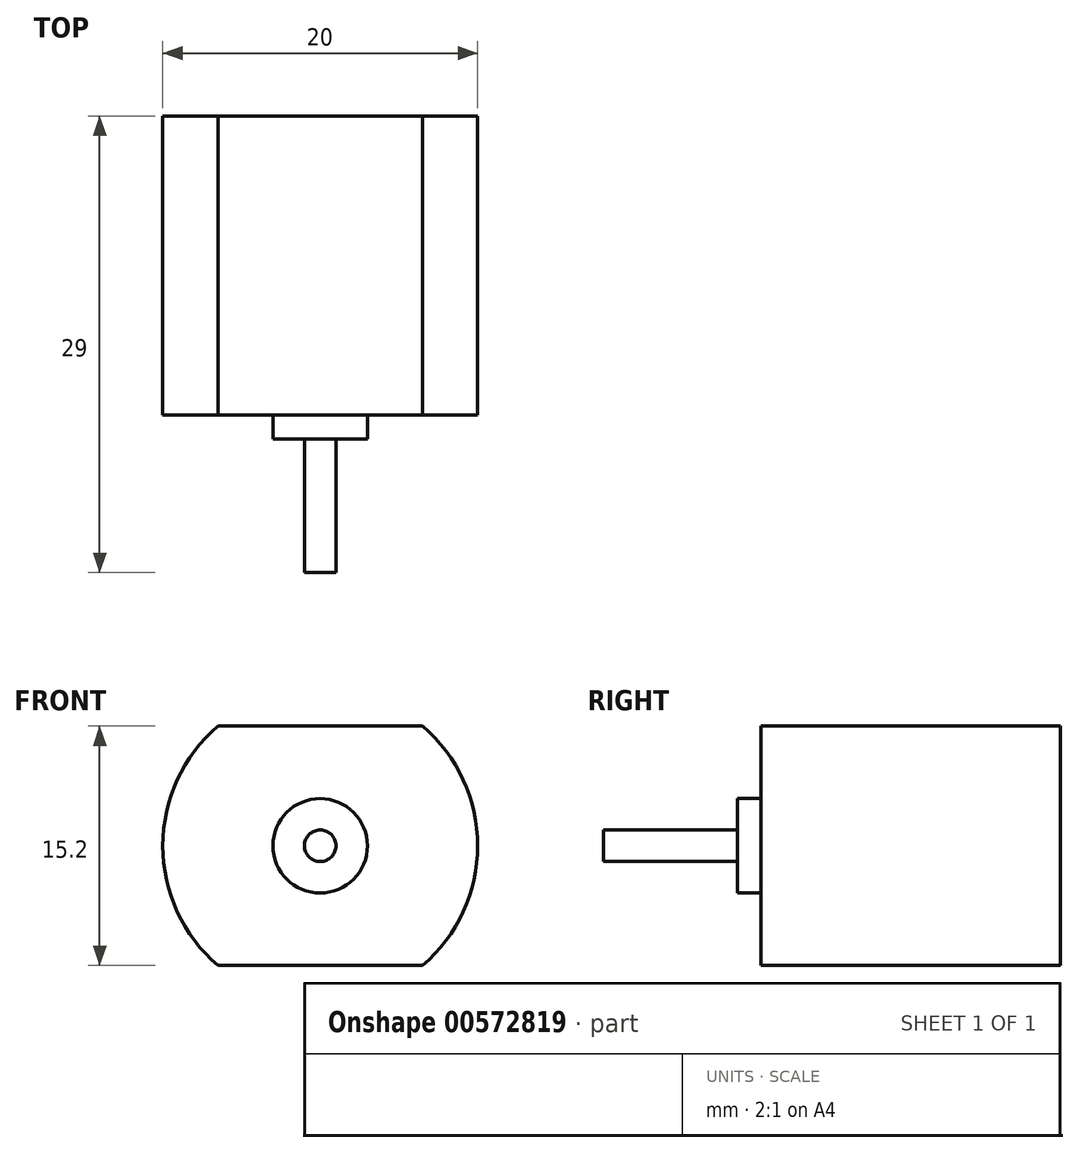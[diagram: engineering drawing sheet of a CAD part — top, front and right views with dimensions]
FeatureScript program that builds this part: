
annotation { "Feature Type Name" : "Feature", "Feature Type Description" : "" }
export const myFeature = defineFeature(function(context is Context, id is Id, definition is map)
    precondition{}
    {
        {
            var Q0;
            Q0=qCreatedBy(makeId("Front.planeOp"),FACE);
            var sketch = newSketch(context, id + "F0", { "sketchPlane" : qUnion([Q0])});
            skArc(sketch, "E0", {"start": v(-6.5, 7.6) * mm, "mid": v(-10, 0) * mm, "end": v(-6.5, -7.6) * mm});
            skLineSegment(sketch, "E1.bottom", {"start": v(6.5, 7.6) * mm, "end": v(-6.5, 7.6) * mm});
            skLineSegment(sketch, "E1.top", {"start": v(6.5, -7.6) * mm, "end": v(-6.5, -7.6) * mm});
            skArc(sketch, "E2.trimOffspring", {"start": v(6.5, -7.6) * mm, "mid": v(10, 0) * mm, "end": v(6.5, 7.6) * mm});
            skSolve(sketch);
        }
        {
            var Q0;
            Q0 = qSketchRegion(id + "F0", true);
            extrude(context, id + "F1", {"entities" : qUnion([Q0]), "depth" : 19 * mm, "offsetDistance" : 25 * mm});
        }
        {
            var Q0;
            Q0=makeQuery(id+"F1.opExtrude","CAP_FACE",FACE,{"disambiguationData":[OSD([sQuery(id+"F0.wireOp",EDGE,"E0"),sQuery(id+"F0.wireOp",EDGE,"E1.bottom"),sQuery(id+"F0.wireOp",EDGE,"E1.top"),sQuery(id+"F0.wireOp",EDGE,"E2.trimOffspring")])],"isStart":false});
            var sketch = newSketch(context, id + "F2", { "sketchPlane" : qUnion([Q0])});
            skCircle(sketch, "E3", {"center": v(0, 0) * mm, "radius": 3 * mm});
            skSolve(sketch);
        }
        {
            var Q0;
            Q0 = qSketchRegion(id + "F2", true);
            extrude(context, id + "F3", {"entities" : qUnion([Q0]), "operationType" : NewBodyOperationType.ADD, "depth" : 1.5 * mm, "offsetDistance" : 25 * mm});
        }
        {
            var Q0;
            Q0=makeQuery(id+"F3.opExtrude","CAP_FACE",FACE,{"disambiguationData":[OSD([sQuery(id+"F2.wireOp",EDGE,"E3")])],"isStart":false});
            var sketch = newSketch(context, id + "F4", { "sketchPlane" : qUnion([Q0])});
            skCircle(sketch, "E4", {"center": v(0, 0) * mm, "radius": 1 * mm});
            skSolve(sketch);
        }
        {
            var Q0;
            Q0 = qSketchRegion(id + "F4", true);
            extrude(context, id + "F5", {"entities" : qUnion([Q0]), "operationType" : NewBodyOperationType.ADD, "depth" : 8.5 * mm, "offsetDistance" : 25 * mm});
        }
    });
